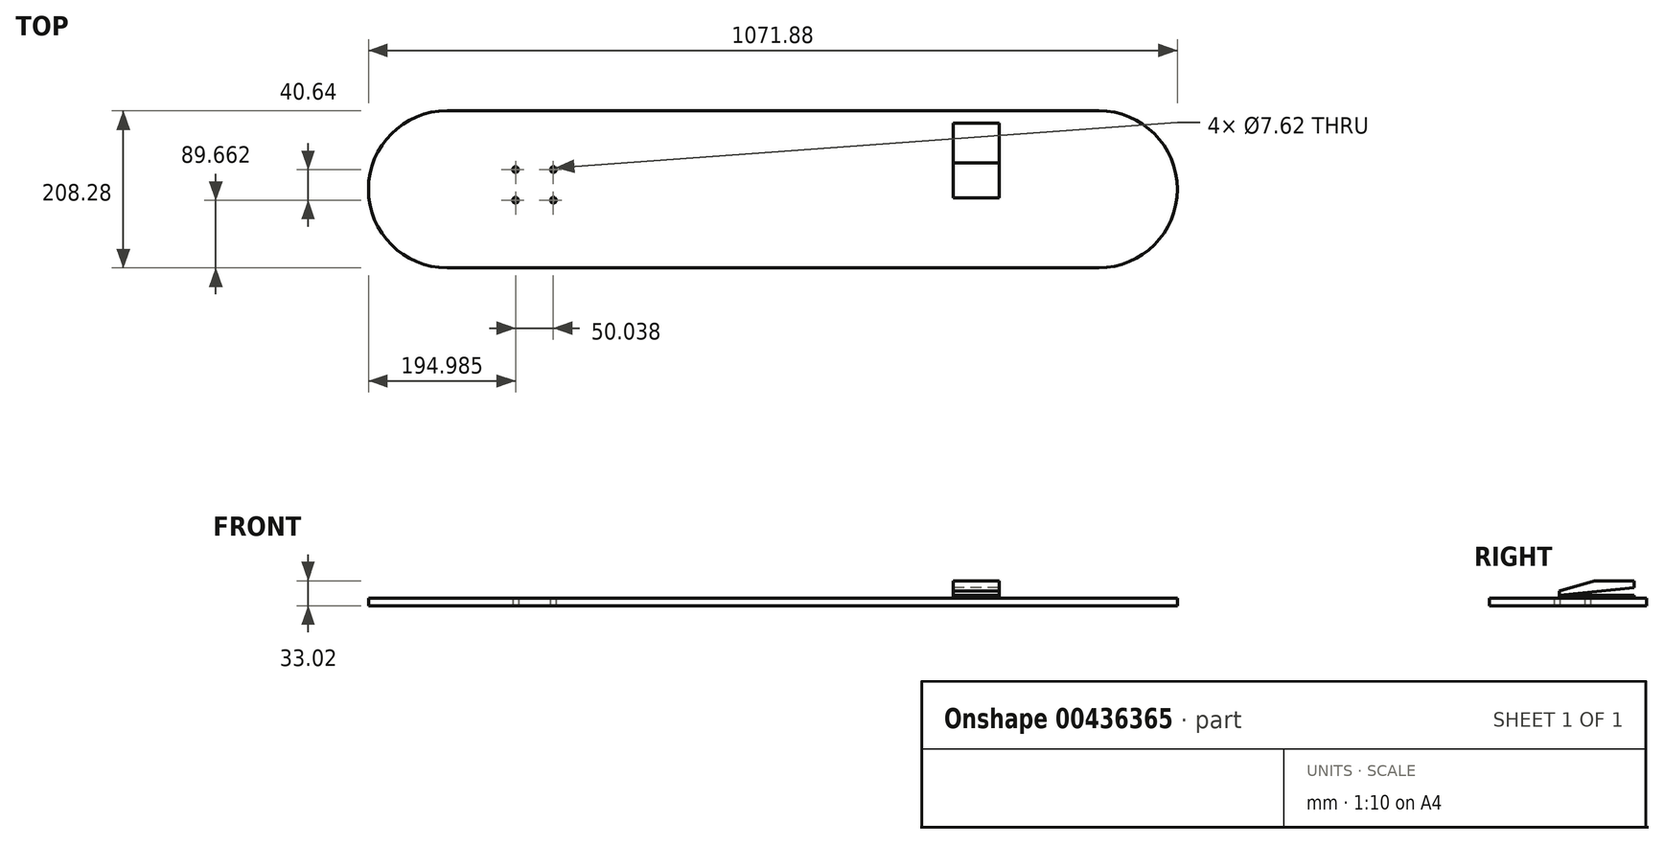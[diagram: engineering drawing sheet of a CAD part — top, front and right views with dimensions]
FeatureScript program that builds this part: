
annotation { "Feature Type Name" : "Feature", "Feature Type Description" : "" }
export const myFeature = defineFeature(function(context is Context, id is Id, definition is map)
    precondition{}
    {
        {
            var Q0;
            Q0=qCreatedBy(makeId("Top.planeOp"),FACE);
            var sketch = newSketch(context, id + "F0", { "sketchPlane" : qUnion([Q0])});
            skLineSegment(sketch, "E0.bottom", {"start": v(-431.8, -104.14) * mm, "end": v(431.8, -104.14) * mm});
            skLineSegment(sketch, "E0.top", {"start": v(-431.8, 104.14) * mm, "end": v(431.8, 104.14) * mm});
            skLineSegment(sketch, "E0.left", {"start": v(-535.94, 0) * mm, "end": v(-535.94, 0) * mm});
            skLineSegment(sketch, "E0.right", {"start": v(535.94, 0) * mm, "end": v(535.94, 0) * mm});
            skPoint(sketch, "E0.middle", {"position": v(0, 0) * mm});
            skPoint(sketch, "E1.visualSharp", {"position": v(-535.94, 104.14) * mm});
            skArc(sketch, "E1.filletArc", {"start": v(-431.8, 104.14) * mm, "mid": v(-505.44, 73.64) * mm, "end": v(-535.94, 0) * mm});
            skPoint(sketch, "E2.visualSharp", {"position": v(-535.94, -104.14) * mm});
            skArc(sketch, "E2.filletArc", {"start": v(-535.94, 0) * mm, "mid": v(-505.44, -73.64) * mm, "end": v(-431.8, -104.14) * mm});
            skPoint(sketch, "E3.visualSharp", {"position": v(535.94, 104.14) * mm});
            skArc(sketch, "E3.filletArc", {"start": v(535.94, 0) * mm, "mid": v(505.44, 73.64) * mm, "end": v(431.8, 104.14) * mm});
            skPoint(sketch, "E4.visualSharp", {"position": v(535.94, -104.14) * mm});
            skArc(sketch, "E4.filletArc", {"start": v(431.8, -104.14) * mm, "mid": v(505.44, -73.64) * mm, "end": v(535.94, 0) * mm});
            skLineSegment(sketch, "E5", {"start": v(-431.8, 104.14) * mm, "end": v(-431.8, -104.14) * mm});
            skLineSegment(sketch, "E6", {"start": v(431.8, 104.14) * mm, "end": v(431.8, -104.14) * mm});
            skCircle(sketch, "E7", {"center": v(-340.96, 26.16) * mm, "radius": 3.81 * mm});
            skLineSegment(sketch, "E8", {"start": v(-340.96, 26.16) * mm, "end": v(-340.96, -14.48) * mm});
            skLineSegment(sketch, "E9", {"start": v(-340.96, 26.16) * mm, "end": v(-290.92, 26.16) * mm});
            skCircle(sketch, "E10", {"center": v(-290.92, 26.16) * mm, "radius": 3.81 * mm});
            skCircle(sketch, "E11", {"center": v(-340.96, -14.48) * mm, "radius": 3.81 * mm});
            skCircle(sketch, "E12", {"center": v(-290.92, -14.48) * mm, "radius": 3.81 * mm});
            skLineSegment(sketch, "E13", {"start": v(-290.92, 26.16) * mm, "end": v(-290.92, -14.48) * mm});
            skSolve(sketch);
        }
        {
            var Q0;
            Q0 = qSketchRegion(id + "F0", true);
            var Q1;
            Q1 = qSketchRegion(id + "F2", true);
            extrude(context, id + "F1", {"entities" : qUnion([Q0, Q1]), "depth" : 10.16 * mm});
        }
        {
            var Q0;
            Q0=qCreatedBy(makeId("Top.planeOp"),FACE);
            var sketch = newSketch(context, id + "F2", { "sketchPlane" : qUnion([Q0])});
            skLineSegment(sketch, "E14.bottom", {"start": v(299.72, -11.43) * mm, "end": v(238.76, -11.43) * mm});
            skLineSegment(sketch, "E14.top", {"start": v(299.72, 87.63) * mm, "end": v(238.76, 87.63) * mm});
            skLineSegment(sketch, "E14.left", {"start": v(299.72, -11.43) * mm, "end": v(299.72, 87.63) * mm});
            skLineSegment(sketch, "E14.right", {"start": v(238.76, -11.43) * mm, "end": v(238.76, 87.63) * mm});
            skPoint(sketch, "E14.middle", {"position": v(269.24, 38.1) * mm});
            skLineSegment(sketch, "E15", {"start": v(0, 0) * mm, "end": v(269.24, 0) * mm});
            skLineSegment(sketch, "E16", {"start": v(269.24, 38.1) * mm, "end": v(269.24, 0) * mm});
            skSolve(sketch);
        }
        {
            var Q0;
            Q0 = qSketchRegion(id + "F2", true);
            extrude(context, id + "F3", {"entities" : qUnion([Q0]), "operationType" : NewBodyOperationType.ADD, "depth" : 33.02 * mm});
        }
        {
            var Q0;
            Q0=qCreatedBy(makeId("Right.planeOp"),FACE);
            var sketch = newSketch(context, id + "F4", { "sketchPlane" : qUnion([Q0])});
            skLineSegment(sketch, "E17", {"start": v(-15.37, 18.3) * mm, "end": v(51.5, 37.78) * mm});
            skLineSegment(sketch, "E18", {"start": v(51.5, 37.78) * mm, "end": v(-16.78, 37.78) * mm});
            skLineSegment(sketch, "E19", {"start": v(-16.78, 37.78) * mm, "end": v(-15.37, 18.3) * mm});
            skLineSegment(sketch, "E20", {"start": v(-12.79, 13.84) * mm, "end": v(93.5, 13.84) * mm});
            skLineSegment(sketch, "E21", {"start": v(93.5, 13.84) * mm, "end": v(93.5, 24.64) * mm});
            skLineSegment(sketch, "E22", {"start": v(-12.79, 13.84) * mm, "end": v(93.5, 24.64) * mm});
            skSolve(sketch);
        }
        {
            var Q0;
            Q0 = qSketchRegion(id + "F4", true);
            extrude(context, id + "F5", {"entities" : qUnion([Q0]), "operationType" : NewBodyOperationType.REMOVE, "depth" : 734.06 * mm});
        }
        {
            var Q0;
            Q0 = qSketchRegion(id + "F0", true);
            extrude(context, id + "F6", {"entities" : qUnion([Q0]), "operationType" : NewBodyOperationType.REMOVE, "oppositeDirection" : true, "depth" : 548.64 * mm});
        }
    });
